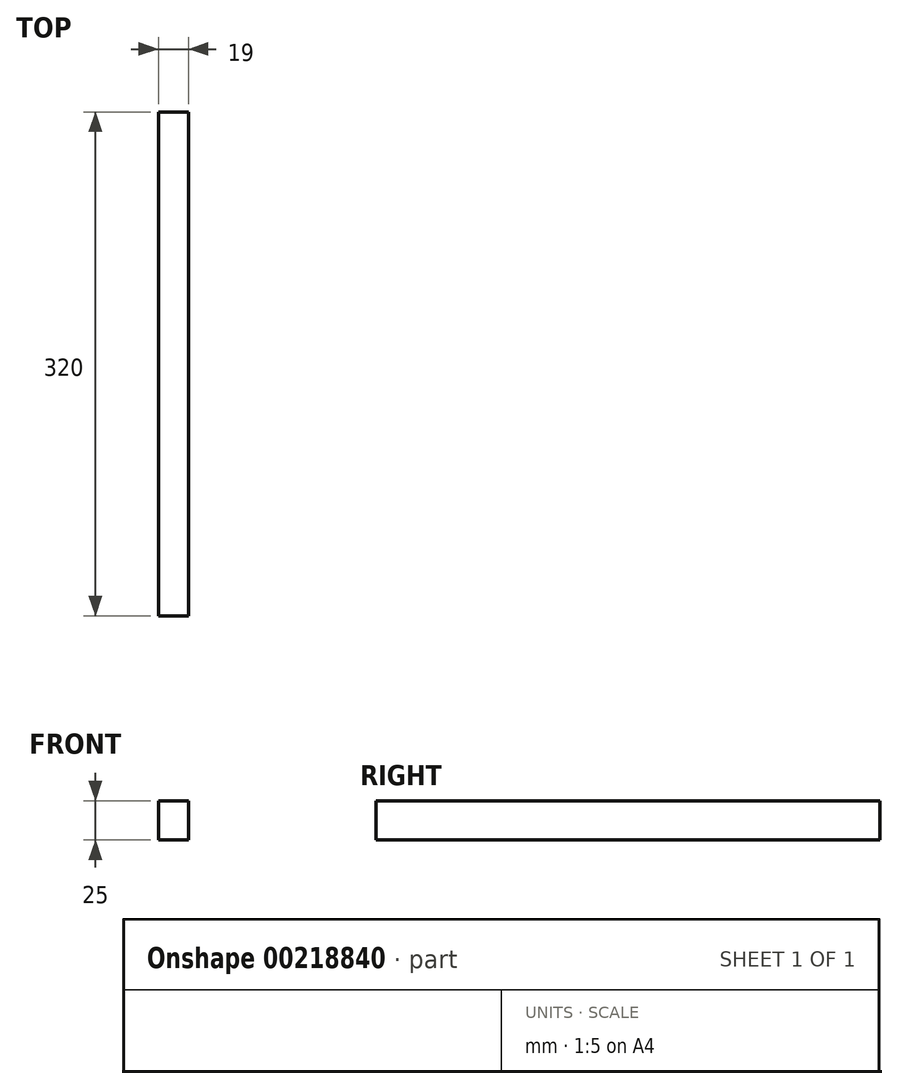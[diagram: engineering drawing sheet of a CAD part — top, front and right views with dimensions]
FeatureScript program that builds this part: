
annotation { "Feature Type Name" : "Feature", "Feature Type Description" : "" }
export const myFeature = defineFeature(function(context is Context, id is Id, definition is map)
    precondition{}
    {
        {
            var Q0;
            Q0=qCreatedBy(makeId("Front.planeOp"),FACE);
            var sketch = newSketch(context, id + "F0", { "sketchPlane" : qUnion([Q0])});
            skLineSegment(sketch, "E0.bottom", {"start": v(-45.39, 26.12) * mm, "end": v(-26.39, 26.12) * mm});
            skLineSegment(sketch, "E0.top", {"start": v(-45.39, 1.12) * mm, "end": v(-26.39, 1.12) * mm});
            skLineSegment(sketch, "E0.left", {"start": v(-45.39, 26.12) * mm, "end": v(-45.39, 1.12) * mm});
            skLineSegment(sketch, "E0.right", {"start": v(-26.39, 26.12) * mm, "end": v(-26.39, 1.12) * mm});
            skSolve(sketch);
        }
        {
            var Q0;
            Q0=makeQuery(id+"F0.imprint","IMPRINT",FACE,{"disambiguationData":[TD([[makeQuery(id+"F0.imprint","IMPRINT",EDGE,{"derivedFrom":sQuery(id+"F0.wireOp",EDGE,"E0.bottom")}),-1.0]])]});
            extrude(context, id + "F1", {"entities" : qUnion([Q0]), "oppositeDirection" : true, "depth" : 320 * mm});
        }
    });
